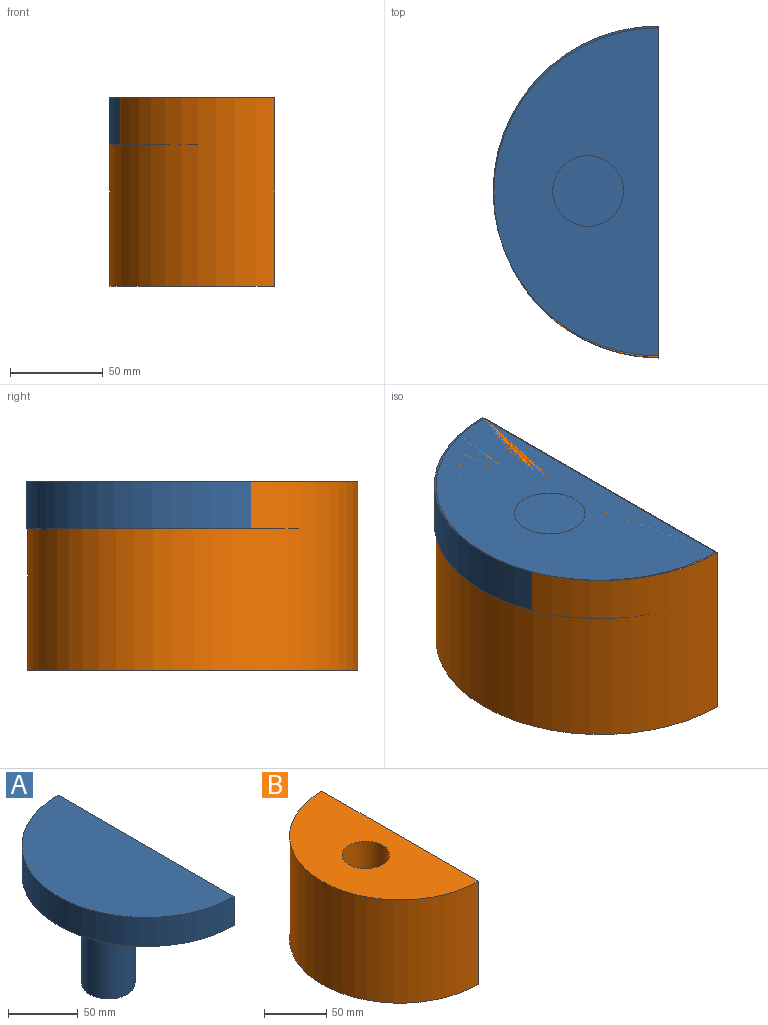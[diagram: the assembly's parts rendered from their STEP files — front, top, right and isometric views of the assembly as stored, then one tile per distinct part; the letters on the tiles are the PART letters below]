
ASSEMBLY  parts=2 mates=1
PART A: 6 faces, bbox 88.9x177.8x101.6 mm
  f0: plane 177.8x25.4mm, normal (1,0,0), area 4516.1mm2, adj f1,f2,f3
  f1: cylinder r=88.9mm len=177.8mm, axis (0,0,-1), area 7093.9mm2, adj f0,f2,f3
  f2: plane 177.8x88.9mm, normal (0,0,1), area 12414.3mm2, adj f0,f1
  f3: plane 177.8x88.9mm, normal (0,0,-1), area 11274.2mm2, adj f0,f1,f4
  f4: cylinder r=19.05mm len=76.2mm, axis (0,0,1), area 9120.7mm2, adj f3,f5
  f5: plane 38.1x38.1mm, normal (0,0,-1), area 1140.1mm2, adj f4
PART B: 5 faces, bbox 88.9x177.8x101.6 mm
  f0: plane 177.8x101.6mm, normal (1,0,0), area 18064.5mm2, adj f2,f3,f4
  f1: cylinder r=19.05mm len=101.6mm, axis (0,0,-1), area 12161mm2, adj f3,f4
  f2: cylinder r=88.9mm len=177.8mm, axis (0,0,-1), area 28375.6mm2, adj f0,f3,f4
  f3: plane 177.8x88.9mm, normal (0,0,1), area 11274.2mm2, adj f0,f1,f2
  f4: plane 177.8x88.9mm, normal (0,0,-1), area 11274.2mm2, adj f0,f1,f2
PLACE A t=(-120.82,65.99,117.78)mm
PLACE B t=(-97.11,36.12,41.58)mm
MATE slider A.f2 <-> B.f1  axis (0,0,1) through (-158.55,65.99,143.18)mm
